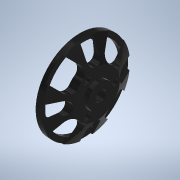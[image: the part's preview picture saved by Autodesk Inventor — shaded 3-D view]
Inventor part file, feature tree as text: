
AUTODESK INVENTOR PART (.ipt)
format: ipt  version: 2022 (Build 260153000, 153)  size: 363,008 bytes
history: native  units: in
note: dims shown in document units (in); Inventor stores cm internally (conversion verified against a paired STEP export)
features: fillet x2, sketch x2, revolve x1, extrude x1
ambient origin geometry x8: Origin, YZ Plane, XZ Plane, XY Plane, X Axis, Y Axis, Z Axis, Center Point
bodies: Solid1 (feature_tree)
feature tree (6):
  revolve  "Revolution1"  [1 undecoded]
  extrude  "Extrusion1"  Depth=0.0197in
  fillet  "Fillet1"  Radius=0.0787in
  fillet  "Fillet2"  Radius=0.2362in
  sketch  "Sketch1"  dims[d0=0.1181in d1=0.8268in]
  sketch  "Sketch2"  dims[d2=0.315in d3=0.4331in d4=0.0787in d5=0.2362in d6=0.0984in d7=360.0deg d8=0.1575in d9=0.0984in d10=0.0295in d11=0.2953in d12=0.1398in d13=0.2165in d15=0.1476in d16=0.2461in d18=45.0deg d19=0.4331in d20=0.5118in d21=0.8661in d22=1.5748in d24=360.0deg d26=0.2362in d27=0.0in d28=0.125in d29=0.0197in d30=0.5906in d31=0.1181in d32=1.1811in d34=360.0deg]
note: 1 required parameter value undecoded (feature->parameter linkage not recoverable at this tier; creation-order binding heuristic only, values carry confidence <= 0.55)
